# Revit family: Geberit iCon Square taharet fonksiyonlu, alçak tip, kapalı formlu asma klozet, Rimfree, klozet kapaklı_PRO_1913965
name_source: partatom
category: Plumbing Fixtures
revit_build: Autodesk Revit 2018 (Build: 20190510_1515(x64)
units: mm (PartAtom-declared; Revit-internal decimal feet)

## family parameters
Always vertical = Yes
Cut with Voids When Loaded = No
OmniClass Number = 23.45.05.21
OmniClass Title = Plumbing Fixtures - Sanitary Disposal Units
Part Type = Normal
Room Calculation Point = Yes
Round Connector Dimension = Use Diameter
Shared = No
Work Plane-Based = No

## types (1)
- 501.671.00.1 Geberit iCon Square taharet fonksiyonlu, alçak tip, kapalı formlu asma klozet, Rimfree, klozet kapaklı
    501671_0_view = Yes
    Application purposes = Gömme rezervuarlar için
    Application range = Plumbing fixture
    Article number key = 501.671.00.1
    BIM Content Version = GEB MG 1.2
    BIM Content revision date = 2020.05.18
    Brand = Geberit
    CW Connection = Yes
    Characteristics = Asma
Alçak tip klozet
Rimfree
Klozetler için EFF2 tipi Geberit duvar montajı ile kolay sabitleme
Tip 1, tam hacim 6 / 5 l, EN 997 uyarınca
4,5 l ile deşarj
Kapalı form
Gizli montaj
Duroplast klozet kapağı
Tam kapanan klozet kapağı
    Description = Geberit iCon Square taharet fonksiyonlu, alçak tip, kapalı formlu asma klozet, Rimfree, klozet kapaklı
    EAN code basic data = 4025410536853
    GEB_culture = tr-TR
    GEB_generic_description = Bathroom collection
    GEB_generic_manufacturer = generic
    GEB_pimversion = 22.02.12
    GEB_processing_type = T
    GEB_reference = PRO_1913965
    GEB_translations = {"ATT_10673":"EAN code basic data","ATT_10882":"Malzeme","ATT_459792":"Renk / Yüzey","applicationPurposes":"Application purposes","application_range":"Application range","brandName":"Brand","characteristics":"Characteristics","content_creator":"BIM Content creator","content_date_changed":"BIM Content revision date","content_version":"BIM Content Version","key 1000":"Article number key","name":"Name","productBrand":"Product brand","scopeOfDelivery":"Scope of delivery","type":"Type","fixed_material":"Main material"}
    HW Connection = No
    IfcDescription = Geberit iCon Square taharet fonksiyonlu, alçak tip, kapalı formlu asma klozet, Rimfree, klozet kapaklı
    IfcExportAs = IfcSanitaryTerminal
    IfcExportType = TOILETPAN
    LOD300 = No
    LOD400 = Yes
    Main material = Geberit, Plastic, Opaque white
    Malzeme = Seramik
    Manufacturer = Geberit
    Name = Geberit iCon Square taharet fonksiyonlu, alçak tip, kapalı formlu asma klozet, Rimfree, klozet kapaklı
    Renk / Yüzey = Beyaz
    Scope of delivery = Önceden monte edilmiş bide nozullu klozet seramiği
Taharet fonksiyonlu klozetler için sifon borusu
Esnek bağlantı borusu
Klozet kapağı
Sabitleme malzemesi
    Vent Connection = No
    Waste Connection = Yes
    outlet_flow = 0.0 L/s

## geometry (parser evidence)
native form markers: Blend x8, Sweep x10
no freeform markers — native parametric forms only
